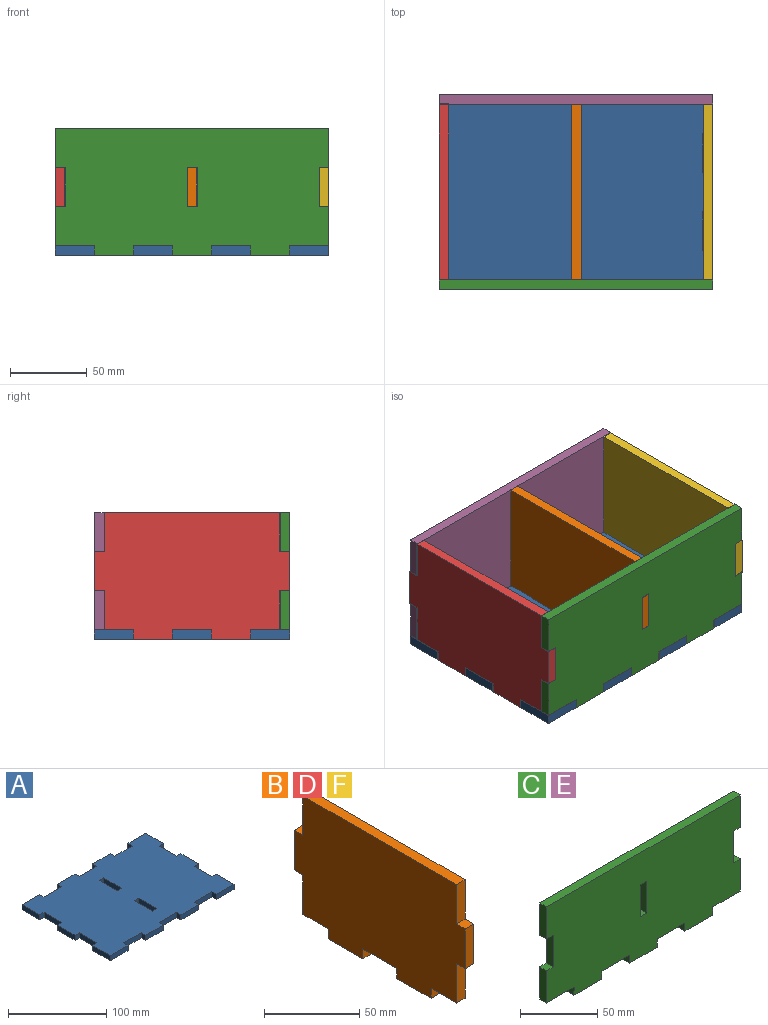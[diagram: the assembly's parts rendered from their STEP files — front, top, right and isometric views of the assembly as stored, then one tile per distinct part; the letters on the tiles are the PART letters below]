
ASSEMBLY  parts=6 mates=5
PART A: 54 faces, bbox 177.8x127x6.4 mm
  f0: plane 6.35x6.26mm, normal (1,0,0), area 39.8mm2, adj f1,f43,f44,f45
  f1: plane 25.22x6.35mm, normal (0,-1,0), area 160.2mm2, adj f0,f2,f44,f45
  f2: plane 6.35x6.26mm, normal (-1,0,0), area 39.8mm2, adj f1,f3,f44,f45
  f3: plane 25.49x6.35mm, normal (0,-1,0), area 161.9mm2, adj f2,f4,f44,f45
  f4: plane 25.49x6.35mm, normal (1,0,0), area 161.9mm2, adj f3,f5,f44,f45
  f5: plane 6.35x6.26mm, normal (0,1,0), area 39.8mm2, adj f4,f6,f44,f45
  f6: plane 25.22x6.35mm, normal (1,0,0), area 160.2mm2, adj f5,f7,f44,f45
  f7: plane 6.35x6.26mm, normal (0,-1,0), area 39.8mm2, adj f6,f8,f44,f45
  f8: plane 25.58x6.35mm, normal (1,0,0), area 162.4mm2, adj f7,f9,f44,f45
  f9: plane 6.35x6.26mm, normal (0,1,0), area 39.8mm2, adj f8,f10,f44,f45
  f10: plane 25.22x6.35mm, normal (1,0,0), area 160.2mm2, adj f9,f11,f44,f45
  f11: plane 6.35x6.26mm, normal (0,-1,0), area 39.8mm2, adj f10,f12,f44,f45
  f12: plane 25.49x6.35mm, normal (1,0,0), area 161.9mm2, adj f11,f13,f44,f45
  f13: plane 25.49x6.35mm, normal (0,1,0), area 161.9mm2, adj f12,f14,f44,f45
  f14: plane 6.35x6.26mm, normal (-1,0,0), area 39.8mm2, adj f13,f15,f44,f45
  f15: plane 25.22x6.35mm, normal (0,1,0), area 160.2mm2, adj f14,f16,f44,f45
  f16: plane 6.35x6.26mm, normal (1,0,0), area 39.8mm2, adj f15,f17,f44,f45
  f17: plane 25.58x6.35mm, normal (0,1,0), area 162.4mm2, adj f16,f18,f44,f45
  f18: plane 6.35x6.26mm, normal (-1,0,0), area 39.8mm2, adj f17,f19,f44,f45
  f19: plane 25.22x6.35mm, normal (0,1,0), area 160.2mm2, adj f18,f20,f44,f45
  f20: plane 6.35x6.26mm, normal (1,0,0), area 39.8mm2, adj f19,f21,f44,f45
  f21: plane 25.58x6.35mm, normal (0,1,0), area 162.4mm2, adj f20,f22,f44,f45
  f22: plane 6.35x6.26mm, normal (-1,0,0), area 39.8mm2, adj f21,f23,f44,f45
  f23: plane 25.22x6.35mm, normal (0,1,0), area 160.2mm2, adj f22,f24,f44,f45
  f24: plane 6.35x6.26mm, normal (1,0,0), area 39.8mm2, adj f23,f25,f44,f45
  f25: plane 25.49x6.35mm, normal (0,1,0), area 161.9mm2, adj f24,f26,f44,f45
  f26: plane 25.49x6.35mm, normal (-1,0,0), area 161.9mm2, adj f25,f27,f44,f45
  f27: plane 6.35x6.26mm, normal (0,-1,0), area 39.8mm2, adj f26,f28,f44,f45
  f28: plane 25.22x6.35mm, normal (-1,0,0), area 160.2mm2, adj f27,f29,f44,f45
  f29: plane 6.35x6.26mm, normal (0,1,0), area 39.8mm2, adj f28,f30,f44,f45
  f30: plane 25.58x6.35mm, normal (-1,0,0), area 162.4mm2, adj f29,f31,f44,f45
  f31: plane 6.35x6.26mm, normal (0,-1,0), area 39.8mm2, adj f30,f32,f44,f45
  f32: plane 25.22x6.35mm, normal (-1,0,0), area 160.2mm2, adj f31,f33,f44,f45
  f33: plane 6.35x6.26mm, normal (0,1,0), area 39.8mm2, adj f32,f34,f44,f45
  f34: plane 25.49x6.35mm, normal (-1,0,0), area 161.9mm2, adj f33,f35,f44,f45
  f35: plane 25.49x6.35mm, normal (0,-1,0), area 161.9mm2, adj f34,f36,f44,f45
  f36: plane 6.35x6.26mm, normal (1,0,0), area 39.8mm2, adj f35,f37,f44,f45
  f37: plane 25.22x6.35mm, normal (0,-1,0), area 160.2mm2, adj f36,f38,f44,f45
  f38: plane 6.35x6.26mm, normal (-1,0,0), area 39.8mm2, adj f37,f39,f44,f45
  f39: plane 25.58x6.35mm, normal (0,-1,0), area 162.4mm2, adj f38,f40,f44,f45
  f40: plane 6.35x6.26mm, normal (1,0,0), area 39.8mm2, adj f39,f41,f44,f45
  f41: plane 25.22x6.35mm, normal (0,-1,0), area 160.2mm2, adj f40,f42,f44,f45
  f42: plane 6.35x6.26mm, normal (-1,0,0), area 39.8mm2, adj f41,f43,f44,f45
  f43: plane 25.58x6.35mm, normal (0,-1,0), area 162.4mm2, adj f0,f42,f44,f45
  f44: plane 177.8x127mm, normal (0,0,1), area 20685.7mm2, adj f0,f1,f2,f3,f4,f5,f6,f7
  f45: plane 177.8x127mm, normal (0,0,-1), area 20685.7mm2, adj f0,f1,f2,f3,f4,f5,f6,f7
  f46: plane 25.58x6.35mm, normal (1,0,0), area 162.4mm2, adj f44,f45,f47,f49
  f47: plane 6.35x6.17mm, normal (0,1,0), area 39.2mm2, adj f44,f45,f46,f48
  f48: plane 25.58x6.35mm, normal (-1,0,0), area 162.4mm2, adj f44,f45,f47,f49
  f49: plane 6.35x6.17mm, normal (0,-1,0), area 39.2mm2, adj f44,f45,f46,f48
  f50: plane 25.58x6.35mm, normal (1,0,0), area 162.4mm2, adj f44,f45,f51,f53
  f51: plane 6.35x6.17mm, normal (0,1,0), area 39.2mm2, adj f44,f45,f50,f52
  f52: plane 25.58x6.35mm, normal (-1,0,0), area 162.4mm2, adj f44,f45,f51,f53
  f53: plane 6.35x6.17mm, normal (0,-1,0), area 39.2mm2, adj f44,f45,f50,f52
PART B: 22 faces, bbox 6.4x127.2x82.6 mm
  f0: plane 6.44x6.35mm, normal (0,0,-1), area 40.9mm2, adj f1,f19,f20,f21
  f1: plane 25.31x6.35mm, normal (0,-1,0), area 160.7mm2, adj f0,f2,f20,f21
  f2: plane 18.96x6.35mm, normal (0,0,-1), area 120.4mm2, adj f1,f3,f20,f21
  f3: plane 6.44x6.35mm, normal (0,-1,0), area 40.9mm2, adj f2,f4,f20,f21
  f4: plane 25.58x6.35mm, normal (0,0,-1), area 162.4mm2, adj f3,f5,f20,f21
  f5: plane 6.44x6.35mm, normal (0,1,0), area 40.9mm2, adj f4,f6,f20,f21
  f6: plane 25.22x6.35mm, normal (0,0,-1), area 160.2mm2, adj f5,f7,f20,f21
  f7: plane 6.44x6.35mm, normal (0,-1,0), area 40.9mm2, adj f6,f8,f20,f21
  f8: plane 25.58x6.35mm, normal (0,0,-1), area 162.4mm2, adj f7,f9,f20,f21
  f9: plane 6.44x6.35mm, normal (0,1,0), area 40.9mm2, adj f8,f10,f20,f21
  f10: plane 18.96x6.35mm, normal (0,0,-1), area 120.4mm2, adj f9,f11,f20,f21
  f11: plane 25.31x6.35mm, normal (0,1,0), area 160.7mm2, adj f10,f12,f20,f21
  f12: plane 6.44x6.35mm, normal (0,0,-1), area 40.9mm2, adj f11,f13,f20,f21
  f13: plane 25.58x6.35mm, normal (0,1,0), area 162.4mm2, adj f12,f14,f20,f21
  f14: plane 6.44x6.35mm, normal (0,0,1), area 40.9mm2, adj f13,f15,f20,f21
  f15: plane 25.31x6.35mm, normal (0,1,0), area 160.7mm2, adj f14,f16,f20,f21
  f16: plane 114.3x6.35mm, normal (0,0,1), area 725.8mm2, adj f15,f17,f20,f21
  f17: plane 25.31x6.35mm, normal (0,-1,0), area 160.7mm2, adj f16,f18,f20,f21
  f18: plane 6.44x6.35mm, normal (0,0,1), area 40.9mm2, adj f17,f19,f20,f21
  f19: plane 25.58x6.35mm, normal (0,-1,0), area 162.4mm2, adj f0,f18,f20,f21
  f20: plane 127.18x82.64mm, normal (1,0,0), area 9368.4mm2, adj f0,f1,f2,f3,f4,f5,f6,f7
  f21: plane 127.18x82.64mm, normal (-1,0,0), area 9368.4mm2, adj f0,f1,f2,f3,f4,f5,f6,f7
PART C: 30 faces, bbox 177.8x6.4x82.6 mm
  f0: plane 6.35x6.26mm, normal (0,0,-1), area 39.8mm2, adj f1,f27,f28,f29
  f1: plane 25.49x6.35mm, normal (1,0,0), area 161.9mm2, adj f0,f2,f28,f29
  f2: plane 177.8x6.35mm, normal (0,0,1), area 1129mm2, adj f1,f3,f28,f29
  f3: plane 25.49x6.35mm, normal (-1,0,0), area 161.9mm2, adj f2,f4,f28,f29
  f4: plane 6.35x6.26mm, normal (0,0,-1), area 39.8mm2, adj f3,f5,f28,f29
  f5: plane 25.22x6.35mm, normal (-1,0,0), area 160.2mm2, adj f4,f6,f28,f29
  f6: plane 6.35x6.26mm, normal (0,0,1), area 39.8mm2, adj f5,f7,f28,f29
  f7: plane 25.49x6.35mm, normal (-1,0,0), area 161.9mm2, adj f6,f8,f28,f29
  f8: plane 25.31x6.35mm, normal (0,0,-1), area 160.7mm2, adj f7,f9,f28,f29
  f9: plane 6.44x6.35mm, normal (-1,0,0.02), area 40.9mm2, adj f8,f10,f28,f29
  f10: plane 25.58x6.35mm, normal (0,0,-1), area 162.4mm2, adj f9,f11,f28,f29
  f11: plane 6.44x6.35mm, normal (1,0,-0.02), area 40.9mm2, adj f10,f12,f28,f29
  f12: plane 25.22x6.35mm, normal (0,0,-1), area 160.2mm2, adj f11,f13,f28,f29
  f13: plane 6.44x6.35mm, normal (-1,0,0), area 40.9mm2, adj f12,f14,f28,f29
  f14: plane 25.58x6.35mm, normal (0,0,-1), area 162.4mm2, adj f13,f15,f28,f29
  f15: plane 6.44x6.35mm, normal (1,0,0), area 40.9mm2, adj f14,f16,f28,f29
  f16: plane 25.22x6.35mm, normal (0,0,-1), area 160.2mm2, adj f15,f17,f28,f29
  f17: plane 6.44x6.35mm, normal (-1,0,0), area 40.9mm2, adj f16,f18,f28,f29
  f18: plane 25.58x6.35mm, normal (0,0,-1), area 162.4mm2, adj f17,f19,f28,f29
  f19: plane 6.44x6.35mm, normal (1,0,0), area 40.9mm2, adj f18,f20,f28,f29
  f20: plane 25.31x6.35mm, normal (0,0,-1), area 160.7mm2, adj f19,f21,f28,f29
  f21: plane 25.49x6.35mm, normal (1,0,0), area 161.9mm2, adj f20,f22,f28,f29
  f22: plane 6.35x6.26mm, normal (0,0,1), area 39.8mm2, adj f21,f27,f28,f29
  f23: plane 6.35x5.99mm, normal (0,0,1), area 38.1mm2, adj f24,f26,f28,f29
  f24: plane 25.22x6.35mm, normal (1,0,0), area 160.2mm2, adj f23,f25,f28,f29
  f25: plane 6.35x5.99mm, normal (0,0,-1), area 38.1mm2, adj f24,f26,f28,f29
  f26: plane 25.22x6.35mm, normal (-1,0,0), area 160.2mm2, adj f23,f25,f28,f29
  f27: plane 25.22x6.35mm, normal (1,0,0), area 160.2mm2, adj f0,f22,f28,f29
  f28: plane 177.8x82.64mm, normal (0,-1,0), area 13575.4mm2, adj f0,f1,f2,f3,f4,f5,f6,f7
  f29: plane 177.8x82.64mm, normal (0,1,0), area 13575.4mm2, adj f0,f1,f2,f3,f4,f5,f6,f7
PART D: same geometry as B
PART E: same geometry as C
PART F: same geometry as B
PLACE A t=(53.03,80.4,-6.35)mm
PLACE B t=(86.08,6.35,0.27)mm
PLACE C t=(0.18,6.26,0.09)mm
PLACE D t=(-0.09,6.53,0.09)mm
PLACE E t=(0.34,127.09,0.09)mm
PLACE F t=(171.72,6.35,-0.09)mm
MATE fastened E.f10 <-> A.f45  axis (0,0,1) through (25.49,120.74,-6.35)mm
MATE fastened C.f18 <-> A.f45  axis (0,0,-1) through (127.09,6.26,-6.35)mm
MATE fastened D.f4 <-> A.f45  axis (0,0,1) through (6.26,25.49,-6.35)mm
MATE fastened F.f18 <-> C.f0  axis (0,0,1) through (171.72,-0.09,50.8)mm
MATE fastened C.f28 <-> B.f19  axis (0,-1,0) through (86.08,-0.09,25.58)mm
